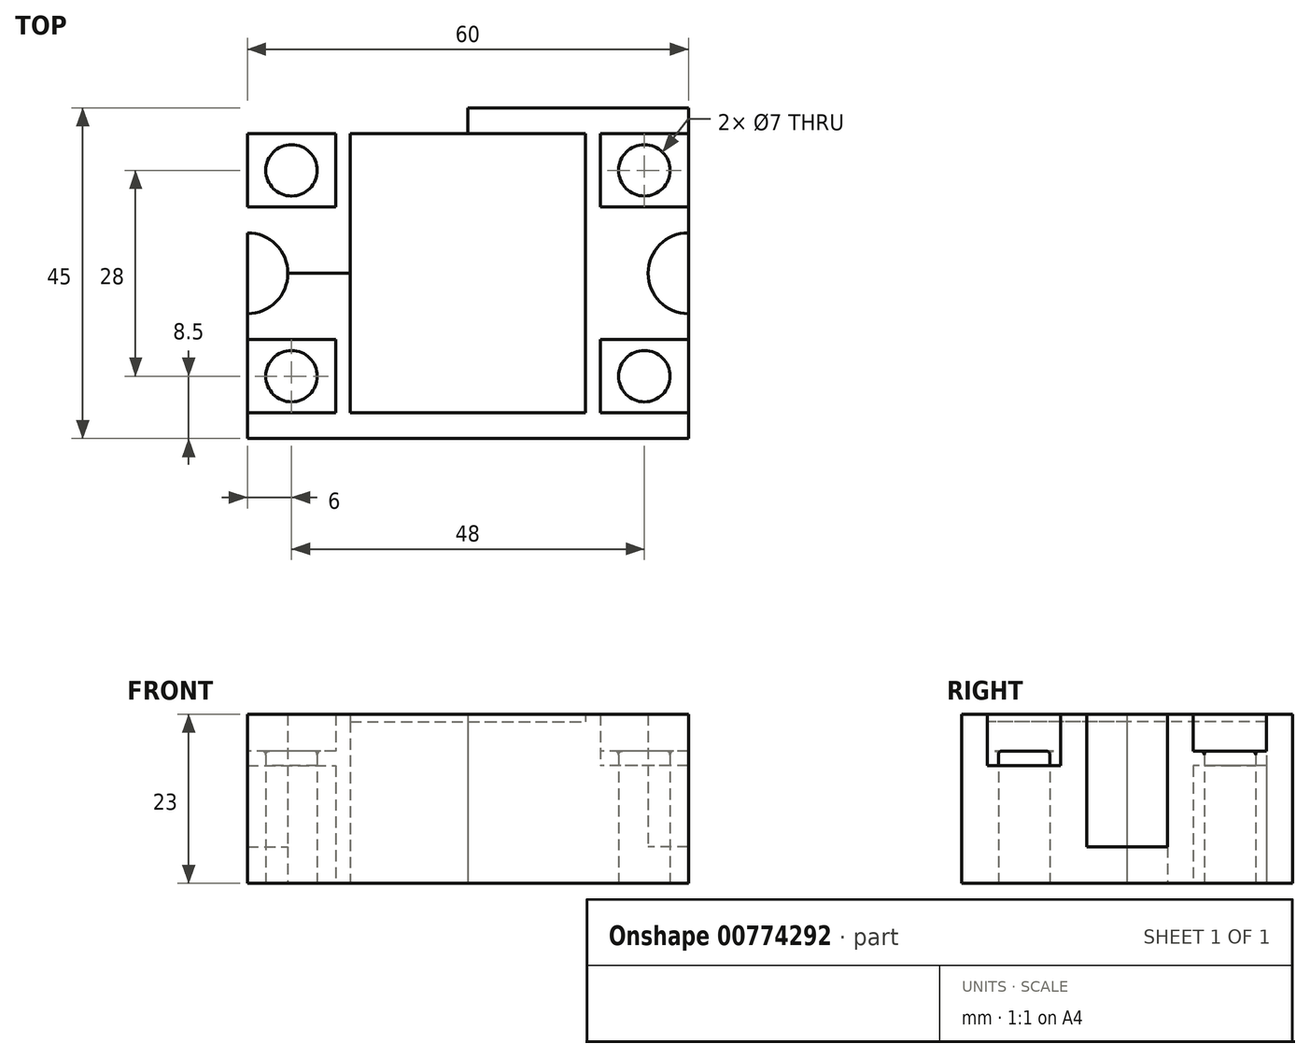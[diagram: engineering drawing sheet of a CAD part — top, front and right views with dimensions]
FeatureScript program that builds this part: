
annotation { "Feature Type Name" : "Feature", "Feature Type Description" : "" }
export const myFeature = defineFeature(function(context is Context, id is Id, definition is map)
    precondition{}
    {
        {
            var Q0;
            Q0=qCreatedBy(makeId("Top.planeOp"),FACE);
            var sketch = newSketch(context, id + "F0", { "sketchPlane" : qUnion([Q0])});
            skLineSegment(sketch, "E0", {"start": v(0, 45) * mm, "end": v(60, 45) * mm});
            skLineSegment(sketch, "E1", {"start": v(60, 45) * mm, "end": v(60, 0) * mm});
            skLineSegment(sketch, "E2", {"start": v(60, 0) * mm, "end": v(0, 0) * mm});
            skLineSegment(sketch, "E3", {"start": v(0, 45) * mm, "end": v(0, 0) * mm});
            skLineSegment(sketch, "E4", {"start": v(0, 45) * mm, "end": v(0, 41.5) * mm});
            skLineSegment(sketch, "E5", {"start": v(0, 41.5) * mm, "end": v(12, 41.5) * mm});
            skLineSegment(sketch, "E6", {"start": v(12, 41.5) * mm, "end": v(12, 31.5) * mm});
            skLineSegment(sketch, "E7", {"start": v(12, 31.5) * mm, "end": v(0, 31.5) * mm});
            skArc(sketch, "E8", {"start": v(0, 28) * mm, "mid": v(5.5, 22.5) * mm, "end": v(0, 17) * mm});
            skLineSegment(sketch, "E9", {"start": v(0, 22.5) * mm, "end": v(60, 22.5) * mm});
            skLineSegment(sketch, "E10.MirrorCS", {"start": v(12, 13.5) * mm, "end": v(0, 13.5) * mm});
            skLineSegment(sketch, "E11.MirrorCS", {"start": v(0, 3.5) * mm, "end": v(12, 3.5) * mm});
            skLineSegment(sketch, "E12.MirrorCS", {"start": v(12, 3.5) * mm, "end": v(12, 13.5) * mm});
            skLineSegment(sketch, "E13", {"start": v(30, 45) * mm, "end": v(30, 0) * mm});
            skLineSegment(sketch, "E14.MirrorCS", {"start": v(48, 41.5) * mm, "end": v(48, 31.5) * mm});
            skLineSegment(sketch, "E15.MirrorCS", {"start": v(60, 41.5) * mm, "end": v(48, 41.5) * mm});
            skLineSegment(sketch, "E16.MirrorCS", {"start": v(48, 31.5) * mm, "end": v(60, 31.5) * mm});
            skArc(sketch, "E17.MirrorCS", {"start": v(60, 28) * mm, "mid": v(54.5, 22.5) * mm, "end": v(60, 17) * mm});
            skLineSegment(sketch, "E18.MirrorCS", {"start": v(48, 13.5) * mm, "end": v(60, 13.5) * mm});
            skLineSegment(sketch, "E19.MirrorCS", {"start": v(48, 3.5) * mm, "end": v(48, 13.5) * mm});
            skLineSegment(sketch, "E20.MirrorCS", {"start": v(60, 3.5) * mm, "end": v(48, 3.5) * mm});
            skLineSegment(sketch, "E21.0", {"start": v(14, 41.5) * mm, "end": v(14, 31.5) * mm});
            skLineSegment(sketch, "E22.0", {"start": v(46, 41.5) * mm, "end": v(46, 31.5) * mm});
            skLineSegment(sketch, "E23", {"start": v(14, 41.5) * mm, "end": v(46, 41.5) * mm});
            skLineSegment(sketch, "E24.0", {"start": v(14, 3.5) * mm, "end": v(14, 13.5) * mm});
            skLineSegment(sketch, "E25.0", {"start": v(46, 3.5) * mm, "end": v(46, 13.5) * mm});
            skLineSegment(sketch, "E26", {"start": v(14, 3.5) * mm, "end": v(46, 3.5) * mm});
            skLineSegment(sketch, "E27", {"start": v(14, 31.5) * mm, "end": v(14, 13.5) * mm});
            skLineSegment(sketch, "E28", {"start": v(46, 31.5) * mm, "end": v(46, 13.5) * mm});
            skLineSegment(sketch, "E29", {"start": v(6, 41.5) * mm, "end": v(6, 31.5) * mm});
            skCircle(sketch, "E30", {"center": v(6, 36.5) * mm, "radius": 3.5 * mm});
            skCircle(sketch, "E31.MirrorC", {"center": v(6, 8.5) * mm, "radius": 3.5 * mm});
            skCircle(sketch, "E32.MirrorC", {"center": v(54, 36.5) * mm, "radius": 3.5 * mm});
            skCircle(sketch, "E33.MirrorC", {"center": v(54, 8.5) * mm, "radius": 3.5 * mm});
            skSolve(sketch);
        }
        {
            var Q0;
            Q0=makeQuery(id+"F0.imprint","IMPRINT",FACE,{"disambiguationData":[TD([[makeQuery(id+"F0.imprint","IMPRINT",EDGE,{"derivedFrom":sQuery(id+"F0.wireOp",EDGE,"E14.MirrorCS")}),-1.0]])]});
            var Q1;
            {var subQ1=sQuery(id+"F0.wireOp",EDGE,"E18.MirrorCS");Q1=makeQuery(id+"F0.imprint","IMPRINT",FACE,{"disambiguationData":[TD([[makeQuery(id+"F0.imprint","IMPRINT",EDGE,{"derivedFrom":subQ1}),1.0]])]});}
            var Q2;
            {var subQ14=sQuery(id+"F0.wireOp",EDGE,"E10.MirrorCS");Q2=makeQuery(id+"F0.imprint","IMPRINT",FACE,{"disambiguationData":[TD([[makeQuery(id+"F0.imprint","IMPRINT",EDGE,{"derivedFrom":subQ14}),-1.0]])]});}
            var Q3;
            {var subQ12=sQuery(id+"F0.wireOp",EDGE,"E4");Q3=makeQuery(id+"F0.imprint","IMPRINT",FACE,{"disambiguationData":[TD([[makeQuery(id+"F0.imprint","IMPRINT",EDGE,{"derivedFrom":subQ12}),1.0]])]});}
            extrude(context, id + "F1", {"entities" : qUnion([Q0, Q1, Q2, Q3]), "depth" : 23 * mm, "offsetDistance" : 25 * mm});
        }
        {
            var Q0;
            {var subQ1=sQuery(id+"F0.wireOp",EDGE,"E21.0");Q0=makeQuery(id+"F0.imprint","IMPRINT",FACE,{"disambiguationData":[TD([[makeQuery(id+"F0.imprint","IMPRINT",EDGE,{"derivedFrom":subQ1}),1.0]])]});}
            var Q1;
            {var subQ1=sQuery(id+"F0.wireOp",EDGE,"E22.0");Q1=makeQuery(id+"F0.imprint","IMPRINT",FACE,{"disambiguationData":[TD([[makeQuery(id+"F0.imprint","IMPRINT",EDGE,{"derivedFrom":subQ1}),-1.0]])]});}
            var Q2;
            {var subQ0=sQuery(id+"F0.wireOp",EDGE,"E25.0");Q2=makeQuery(id+"F0.imprint","IMPRINT",FACE,{"disambiguationData":[TD([[makeQuery(id+"F0.imprint","IMPRINT",EDGE,{"derivedFrom":subQ0}),1.0]])]});}
            var Q3;
            {var subQ0=sQuery(id+"F0.wireOp",EDGE,"E24.0");Q3=makeQuery(id+"F0.imprint","IMPRINT",FACE,{"disambiguationData":[TD([[makeQuery(id+"F0.imprint","IMPRINT",EDGE,{"derivedFrom":subQ0}),-1.0]])]});}
            extrude(context, id + "F2", {"entities" : qUnion([Q0, Q1, Q2, Q3]), "operationType" : NewBodyOperationType.ADD, "depth" : 22 * mm, "offsetDistance" : 25 * mm});
        }
        {
            var Q0;
            {var subQ0=sQuery(id+"F0.wireOp",EDGE,"E7");var subQ1=sQuery(id+"F0.wireOp",EDGE,"E3");var subQ2=makeQuery(id+"F0.imprint","INTERSECT",VERTEX,{"derivedFrom":[subQ1,subQ0]});Q0=makeQuery(id+"F0.imprint","IMPRINT",FACE,{"disambiguationData":[TD([[makeQuery(id+"F0.imprint","IMPRINT",EDGE,{"disambiguationData":[TD([[subQ2,1.0]])],"derivedFrom":subQ0}),-1.0]])]});}
            var Q1;
            {var subQ6=sQuery(id+"F0.wireOp",EDGE,"E6");Q1=makeQuery(id+"F0.imprint","IMPRINT",FACE,{"disambiguationData":[TD([[makeQuery(id+"F0.imprint","IMPRINT",EDGE,{"derivedFrom":subQ6}),-1.0]])]});}
            var Q2;
            {var subQ1=sQuery(id+"F0.wireOp",EDGE,"E10.MirrorCS");Q2=makeQuery(id+"F0.imprint","IMPRINT",FACE,{"disambiguationData":[TD([[makeQuery(id+"F0.imprint","IMPRINT",EDGE,{"derivedFrom":subQ1}),1.0]])]});}
            var Q3;
            Q3=makeQuery(id+"F0.imprint","IMPRINT",FACE,{"disambiguationData":[TD([[makeQuery(id+"F0.imprint","IMPRINT",EDGE,{"derivedFrom":sQuery(id+"F0.wireOp",EDGE,"E14.MirrorCS")}),1.0]])]});
            var Q4;
            {var subQ1=sQuery(id+"F0.wireOp",EDGE,"E18.MirrorCS");Q4=makeQuery(id+"F0.imprint","IMPRINT",FACE,{"disambiguationData":[TD([[makeQuery(id+"F0.imprint","IMPRINT",EDGE,{"derivedFrom":subQ1}),-1.0]])]});}
            extrude(context, id + "F3", {"entities" : qUnion([Q0, Q1, Q2, Q3, Q4]), "operationType" : NewBodyOperationType.ADD, "depth" : 16 * mm, "offsetDistance" : 25 * mm});
        }
        {
            var Q0;
            {var subQ0=sQuery(id+"F0.wireOp",EDGE,"E30");var subQ1=sQuery(id+"F0.wireOp",EDGE,"E29");var subQ2=makeQuery(id+"F0.imprint","INTERSECT",VERTEX,{"disambiguationData":[OD(0.0)],"derivedFrom":[subQ1,subQ0]});Q0=makeQuery(id+"F0.imprint","IMPRINT",FACE,{"disambiguationData":[TD([[makeQuery(id+"F0.imprint","IMPRINT",EDGE,{"disambiguationData":[TD([[subQ2,-1.0]])],"derivedFrom":subQ1}),1.0]])]});}
            var Q1;
            {var subQ0=sQuery(id+"F0.wireOp",EDGE,"E30");var subQ1=sQuery(id+"F0.wireOp",EDGE,"E29");var subQ2=makeQuery(id+"F0.imprint","INTERSECT",VERTEX,{"disambiguationData":[OD(0.0)],"derivedFrom":[subQ1,subQ0]});Q1=makeQuery(id+"F0.imprint","IMPRINT",FACE,{"disambiguationData":[TD([[makeQuery(id+"F0.imprint","IMPRINT",EDGE,{"disambiguationData":[TD([[subQ2,-1.0]])],"derivedFrom":subQ1}),-1.0]])]});}
            var Q2;
            Q2=makeQuery(id+"F0.imprint","IMPRINT",FACE,{"disambiguationData":[TD([[makeQuery(id+"F0.imprint","IMPRINT",EDGE,{"derivedFrom":sQuery(id+"F0.wireOp",EDGE,"E31.MirrorC")}),-1.0]])]});
            var Q3;
            Q3=makeQuery(id+"F0.imprint","IMPRINT",FACE,{"disambiguationData":[TD([[makeQuery(id+"F0.imprint","IMPRINT",EDGE,{"derivedFrom":sQuery(id+"F0.wireOp",EDGE,"E32.MirrorC")}),-1.0]])]});
            var Q4;
            Q4=makeQuery(id+"F0.imprint","IMPRINT",FACE,{"disambiguationData":[TD([[makeQuery(id+"F0.imprint","IMPRINT",EDGE,{"derivedFrom":sQuery(id+"F0.wireOp",EDGE,"E33.MirrorC")}),1.0]])]});
            extrude(context, id + "F4", {"entities" : qUnion([Q0, Q1, Q2, Q3, Q4]), "operationType" : NewBodyOperationType.ADD, "depth" : 18 * mm, "offsetDistance" : 25 * mm});
        }
        {
            var Q0;
            Q0=makeQuery(id+"F4.opExtrude","CAP_EDGE",EDGE,{"disambiguationData":[OSD([sQuery(id+"F0.wireOp",EDGE,"E30")])],"isStart":false});
            var Q1;
            Q1=makeQuery(id+"F4.opExtrude","CAP_EDGE",EDGE,{"disambiguationData":[OSD([sQuery(id+"F0.wireOp",EDGE,"E31.MirrorC")])],"isStart":false});
            var Q2;
            Q2=makeQuery(id+"F4.opExtrude","CAP_EDGE",EDGE,{"disambiguationData":[OSD([sQuery(id+"F0.wireOp",EDGE,"E32.MirrorC")])],"isStart":false});
            var Q3;
            Q3=makeQuery(id+"F4.opExtrude","CAP_EDGE",EDGE,{"disambiguationData":[OSD([sQuery(id+"F0.wireOp",EDGE,"E33.MirrorC")])],"isStart":false});
            fillet(context, id + "F5", {"entities" : qUnion([Q0, Q1, Q2, Q3]), "radius" : .5 * mm, "tangentPropagation" : true, "allowEdgeOverflow" : false});
        }
        {
            var Q0;
            {var subQ0=sQuery(id+"F0.wireOp",EDGE,"E8");var subQ1=sQuery(id+"F0.wireOp",EDGE,"E3");var subQ2=makeQuery(id+"F0.imprint","INTERSECT",VERTEX,{"disambiguationData":[OD(0.0)],"derivedFrom":[subQ1,subQ0]});Q0=makeQuery(id+"F0.imprint","IMPRINT",FACE,{"disambiguationData":[TD([[makeQuery(id+"F0.imprint","IMPRINT",EDGE,{"disambiguationData":[TD([[subQ2,-1.0]])],"derivedFrom":subQ1}),1.0]])]});}
            var Q1;
            {var subQ0=sQuery(id+"F0.wireOp",EDGE,"E8");var subQ1=sQuery(id+"F0.wireOp",EDGE,"E3");var subQ2=makeQuery(id+"F0.imprint","INTERSECT",VERTEX,{"disambiguationData":[OD(1.0)],"derivedFrom":[subQ1,subQ0]});Q1=makeQuery(id+"F0.imprint","IMPRINT",FACE,{"disambiguationData":[TD([[makeQuery(id+"F0.imprint","IMPRINT",EDGE,{"disambiguationData":[TD([[subQ2,1.0]])],"derivedFrom":subQ1}),1.0]])]});}
            var Q2;
            {var subQ0=sQuery(id+"F0.wireOp",EDGE,"E9");var subQ1=sQuery(id+"F0.wireOp",EDGE,"E1");var subQ2=makeQuery(id+"F0.imprint","INTERSECT",VERTEX,{"derivedFrom":[subQ1,subQ0]});Q2=makeQuery(id+"F0.imprint","IMPRINT",FACE,{"disambiguationData":[TD([[makeQuery(id+"F0.imprint","IMPRINT",EDGE,{"disambiguationData":[TD([[subQ2,1.0]])],"derivedFrom":subQ1}),-1.0]])]});}
            var Q3;
            {var subQ0=sQuery(id+"F0.wireOp",EDGE,"E9");var subQ1=sQuery(id+"F0.wireOp",EDGE,"E1");var subQ2=makeQuery(id+"F0.imprint","INTERSECT",VERTEX,{"derivedFrom":[subQ1,subQ0]});Q3=makeQuery(id+"F0.imprint","IMPRINT",FACE,{"disambiguationData":[TD([[makeQuery(id+"F0.imprint","IMPRINT",EDGE,{"disambiguationData":[TD([[subQ2,-1.0]])],"derivedFrom":subQ1}),-1.0]])]});}
            extrude(context, id + "F6", {"entities" : qUnion([Q0, Q1, Q2, Q3]), "operationType" : NewBodyOperationType.ADD, "depth" : 5 * mm, "offsetDistance" : 25 * mm});
        }
    });
